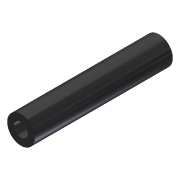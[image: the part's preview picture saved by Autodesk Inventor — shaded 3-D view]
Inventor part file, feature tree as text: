
AUTODESK INVENTOR PART (.ipt)
format: ipt  version: 2013 (Build 170138000, 138)  size: 75,776 bytes
history: native  units: in
note: dims shown in document units (in); Inventor stores cm internally (conversion verified against a paired STEP export)
features: extrude x1, sketch x1
ambient origin geometry x8: Origin, YZ Plane, XZ Plane, XY Plane, X Axis, Y Axis, Z Axis, Center Point
bodies: Solid1 (feature_tree)
feature tree (2):
  extrude  "Extrusion1"  Depth=0.25in
  sketch  "Sketch1"  dims[d0=0.5in d1=0.25in d2=2.5in d3=0.0in]
